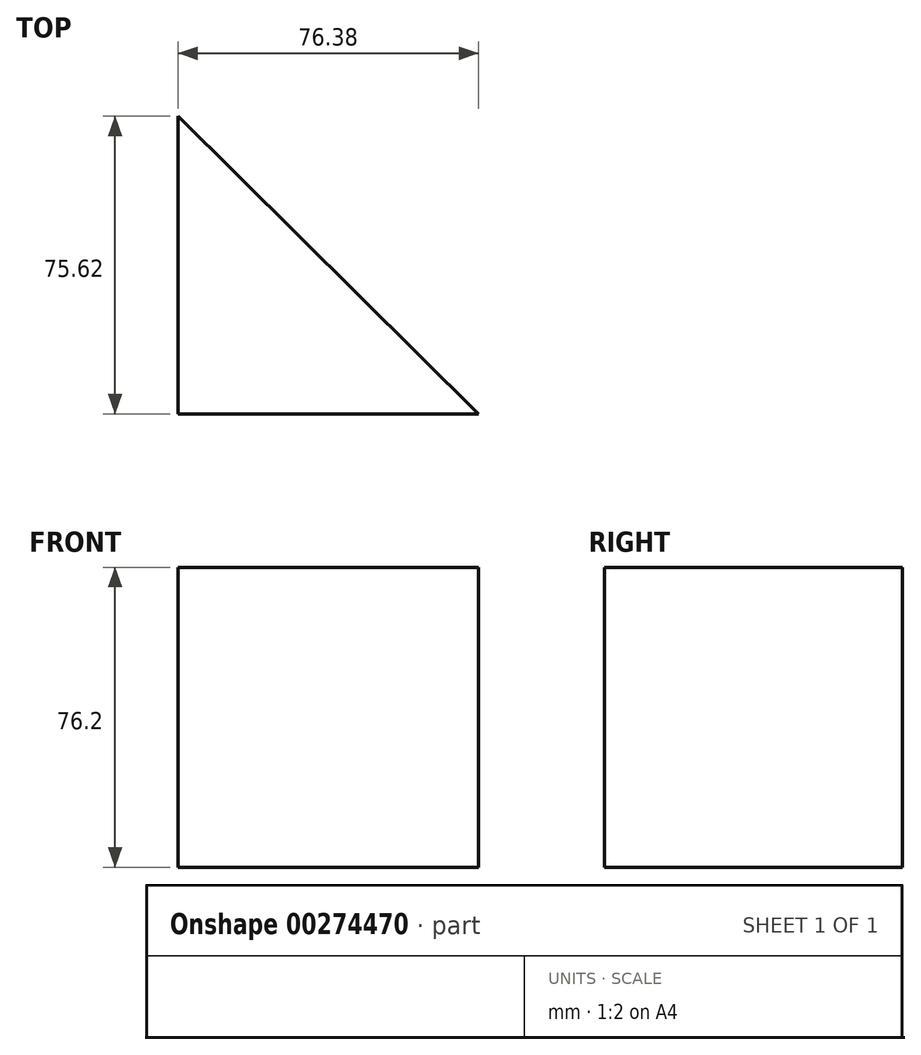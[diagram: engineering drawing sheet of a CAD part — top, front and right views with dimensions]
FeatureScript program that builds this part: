
annotation { "Feature Type Name" : "Feature", "Feature Type Description" : "" }
export const myFeature = defineFeature(function(context is Context, id is Id, definition is map)
    precondition{}
    {
        {
            var Q0;
            Q0=qCreatedBy(makeId("Top.planeOp"),FACE);
            var sketch = newSketch(context, id + "F0", { "sketchPlane" : qUnion([Q0])});
            skLineSegment(sketch, "E0.bottom", {"start": v(0, 0) * mm, "end": v(-76.38, 0) * mm});
            skLineSegment(sketch, "E0.top", {"start": v(0, 75.62) * mm, "end": v(-76.38, 75.62) * mm});
            skLineSegment(sketch, "E0.left", {"start": v(0, 0) * mm, "end": v(0, 75.62) * mm});
            skLineSegment(sketch, "E0.right", {"start": v(-76.38, 0) * mm, "end": v(-76.38, 75.62) * mm});
            skSolve(sketch);
        }
        {
            var Q0;
            Q0 = qSketchRegion(id + "F0", true);
            extrude(context, id + "F1", {"entities" : qUnion([Q0]), "depth" : 76.2 * mm});
        }
        {
            var Q0;
            Q0=makeQuery(id+"F1.opExtrude","CAP_FACE",FACE,{"disambiguationData":[OSD([sQuery(id+"F0.wireOp",EDGE,"E0.bottom"),sQuery(id+"F0.wireOp",EDGE,"E0.top"),sQuery(id+"F0.wireOp",EDGE,"E0.left"),sQuery(id+"F0.wireOp",EDGE,"E0.right")])],"isStart":false});
            var sketch = newSketch(context, id + "F2", { "sketchPlane" : qUnion([Q0])});
            skLineSegment(sketch, "E1", {"start": v(-76.38, 75.62) * mm, "end": v(0, 0) * mm});
            skLineSegment(sketch, "E2", {"start": v(0, 0) * mm, "end": v(0, 75.62) * mm});
            skLineSegment(sketch, "E3", {"start": v(0, 75.62) * mm, "end": v(-76.38, 75.62) * mm});
            skSolve(sketch);
        }
        {
            var Q0;
            Q0 = qSketchRegion(id + "F2", true);
            extrude(context, id + "F3", {"entities" : qUnion([Q0]), "operationType" : NewBodyOperationType.REMOVE, "oppositeDirection" : true, "depth" : 76.2 * mm});
        }
    });
